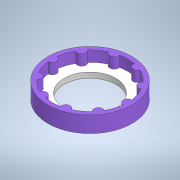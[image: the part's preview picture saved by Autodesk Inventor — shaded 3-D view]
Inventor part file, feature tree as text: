
AUTODESK INVENTOR PART (.ipt)
format: ipt  version: 2022 (Build 260153000, 153)  size: 166,912 bytes
history: native  units: in
note: dims shown in document units (in); Inventor stores cm internally (conversion verified against a paired STEP export)
features: extrude x4, sketch x3
ambient origin geometry x8: Origin, YZ Plane, XZ Plane, XY Plane, X Axis, Y Axis, Z Axis, Center Point
bodies: Solid1 (feature_tree)
feature tree (7):
  sketch  "Sketch1"  dims[d1=2.7559in d2=0.315in]
  extrude  "Extrusion1"  Depth=0.315in
  extrude  "Extrusion2"  Depth=3.0709in
  extrude  "Extrusion3"  Depth=0.3937in TaperAngle=0.0deg
  extrude  "Extrusion4"  Depth=0.3937in
  sketch  "Sketch2"  dims[d3=3.937in d5=360.0deg d7=3.0709in]
  sketch  "Sketch3"  dims[d8=0.1969in d9=0.0in d10=0.3937in d11=0.0in d12=0.3937in d13=0.3937in d14=0.0in d16=0.3937in d17=0.0in d18=1.8898in]
